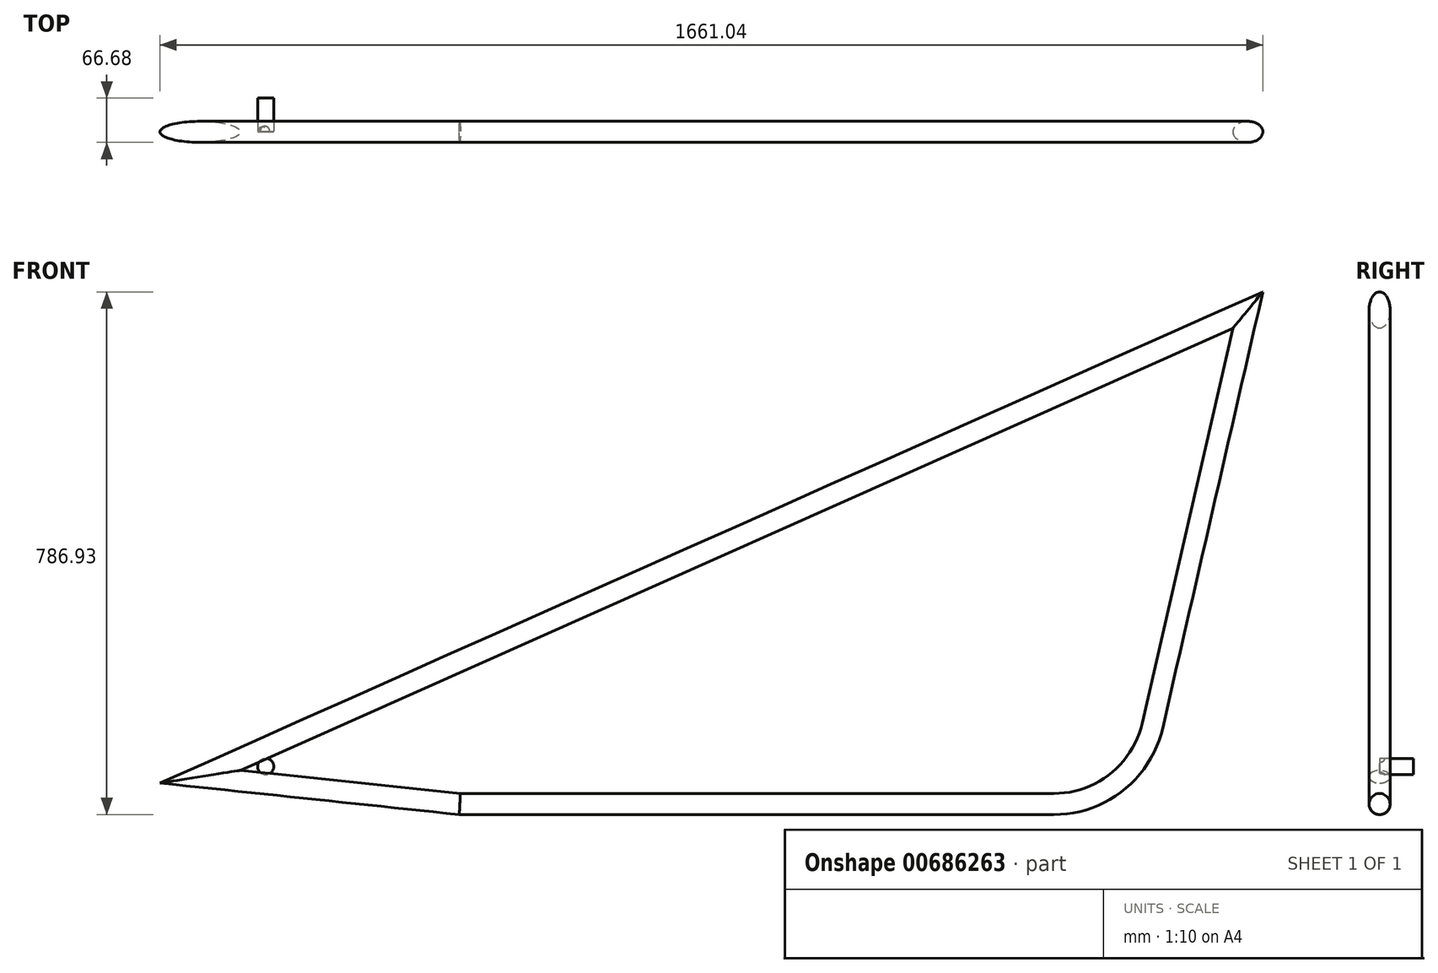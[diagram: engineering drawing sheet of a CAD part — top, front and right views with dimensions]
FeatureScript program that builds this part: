
annotation { "Feature Type Name" : "Feature", "Feature Type Description" : "" }
export const myFeature = defineFeature(function(context is Context, id is Id, definition is map)
    precondition{}
    {
        {
            var Q0;
            Q0=qCreatedBy(makeId("Front.planeOp"),FACE);
            var sketch = newSketch(context, id + "F0", { "sketchPlane" : qUnion([Q0])});
            skLineSegment(sketch, "E0", {"start": v(842.45, 702.52) * mm, "end": v(-735.42, 0) * mm});
            skLineSegment(sketch, "E1", {"start": v(-735.42, 0) * mm, "end": v(-344.34, -41.1) * mm});
            skLineSegment(sketch, "E2", {"start": v(-344.34, -41.1) * mm, "end": v(550.3, -41.1) * mm});
            skLineSegment(sketch, "E3", {"start": v(842.45, 702.52) * mm, "end": v(698.83, 77.18) * mm});
            skPoint(sketch, "E4.visualSharp", {"position": v(671.66, -41.1) * mm});
            skArc(sketch, "E4.filletArc", {"start": v(550.3, -41.1) * mm, "mid": v(645.23, -7.92) * mm, "end": v(698.83, 77.18) * mm});
            skLineSegment(sketch, "E5", {"start": v(-29.69, 314.21) * mm, "end": v(-29.69, -41.1) * mm});
            skSolve(sketch);
        }
        {
            var Q0;
            Q0=qCreatedBy(makeId("Right.planeOp"),FACE);
            var sketch = newSketch(context, id + "F1", { "sketchPlane" : qUnion([Q0])});
            skCircle(sketch, "E6", {"center": v(0, -41.1) * mm, "radius": 15.88 * mm});
            skSolve(sketch);
        }
        {
            var Q0;
            Q0=makeQuery(id+"F1.imprint","IMPRINT",FACE,{"disambiguationData":[TD([[makeQuery(id+"F1.imprint","IMPRINT",EDGE,{"derivedFrom":sQuery(id+"F1.wireOp",EDGE,"E6")}),1.0]])]});
            var Q1;
            Q1=sQuery(id+"F0.wireOp",EDGE,"E2");
            var Q2;
            Q2=sQuery(id+"F0.wireOp",EDGE,"E4.filletArc");
            var Q3;
            Q3=sQuery(id+"F0.wireOp",EDGE,"E3");
            var Q4;
            Q4=sQuery(id+"F0.wireOp",EDGE,"E1");
            var Q5;
            Q5=sQuery(id+"F0.wireOp",EDGE,"E0");
            sweep(context, id + "F2", {"profiles" : qUnion([Q0]), "path" : qUnion([Q1, Q2, Q3, Q4, Q5])});
        }
        {
            var Q0;
            Q0=qCreatedBy(makeId("Front.planeOp"),FACE);
            var sketch = newSketch(context, id + "F3", { "sketchPlane" : qUnion([Q0])});
            skCircle(sketch, "E7", {"center": v(-636.83, 15.45) * mm, "radius": 12.2 * mm});
            skSolve(sketch);
        }
        {
            var Q0;
            Q0=makeQuery(id+"F3.imprint","IMPRINT",FACE,{"disambiguationData":[TD([[makeQuery(id+"F3.imprint","IMPRINT",EDGE,{"derivedFrom":sQuery(id+"F3.wireOp",EDGE,"E7")}),1.0]])]});
            extrude(context, id + "F4", {"entities" : qUnion([Q0]), "operationType" : NewBodyOperationType.ADD, "oppositeDirection" : true, "depth" : 50.8 * mm, "offsetDistance" : 25.4 * mm});
        }
    });
